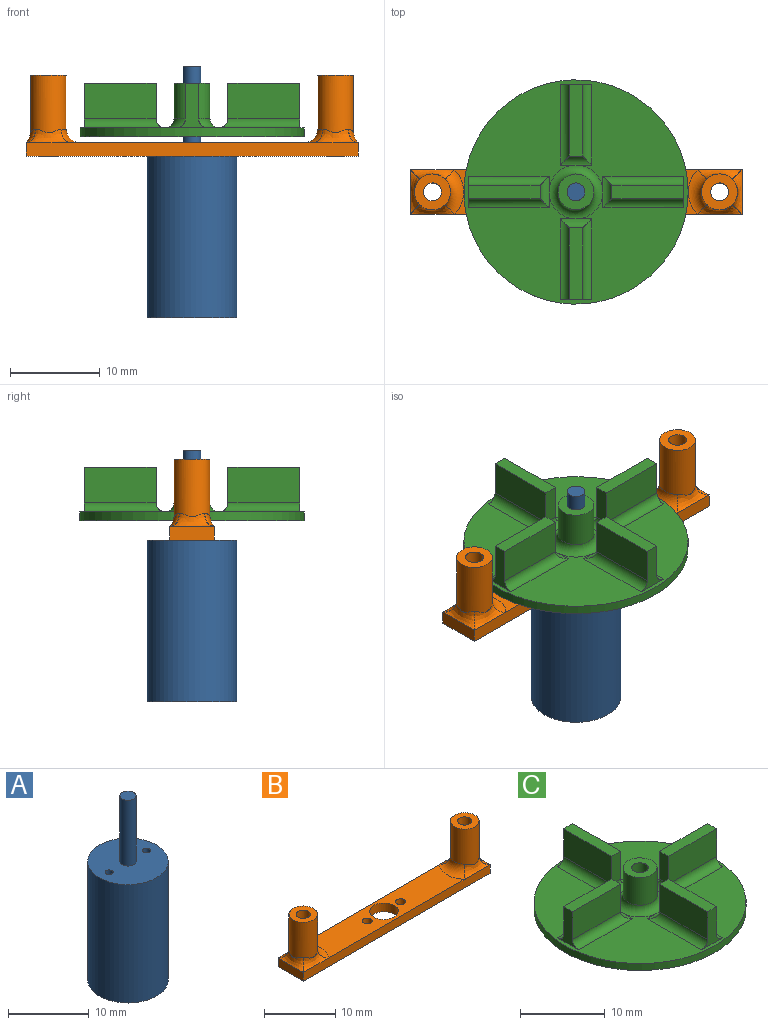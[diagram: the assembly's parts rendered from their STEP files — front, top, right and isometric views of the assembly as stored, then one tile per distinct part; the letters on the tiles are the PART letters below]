
ASSEMBLY  parts=3 mates=4
PART A: 9 faces, bbox 10x10x28 mm
  f0: cylinder r=5mm len=18mm, axis (0,0,-1), area 565.5mm2, adj f1,f2
  f1: plane 10x10mm, normal (0,0,1), area 73.8mm2, adj f0,f3,f5,f7
  f2: plane 10x10mm, normal (0,0,-1), area 78.5mm2, adj f0
  f3: cylinder r=1mm len=10mm, axis (0,0,-1), area 62.8mm2, adj f1,f4
  f4: plane 2x2mm, normal (0,0,1), area 3.1mm2, adj f3
  f5: cylinder r=0.5mm len=3mm, axis (0,0,1), area 9.4mm2, adj f1,f6
  f6: plane 1x1mm, normal (0,0,1), area 0.8mm2, adj f5
  f7: cylinder r=0.5mm len=3mm, axis (0,0,1), area 9.4mm2, adj f1,f8
  f8: plane 1x1mm, normal (0,0,1), area 0.8mm2, adj f7
PART B: 31 faces, bbox 38.7x7.3x9.2 mm
  f0: plane 0.05x0.05mm, normal (0,0,1), area 0mm2, adj f6,f11,f22
  f1: plane 0.05x0.05mm, normal (0,0,1), area 0mm2, adj f5,f6,f19
  f2: plane 0.05x0.05mm, normal (0,0,1), area 0mm2, adj f4,f11,f28
  f3: plane 27.1x5mm, normal (0,0,1), area 112.6mm2, adj f5,f8,f9,f10,f11,f23,f25
  f4: plane 5.2x1.7mm, normal (1,0,0), area 7.5mm2, adj f2,f5,f11,f13,f14,f30
  f5: plane 37.2x1.7mm, normal (0,1,0), area 55.5mm2, adj f1,f3,f4,f6,f13,f14,f21,f27
  f6: plane 5.2x1.7mm, normal (-1,0,0), area 7.5mm2, adj f0,f1,f5,f11,f14,f20
  f7: cylinder r=1mm len=9mm, axis (0,0,-1), area 56.5mm2, adj f14,f18
  f8: cylinder r=0.7mm len=1.5mm, axis (0,0,-1), area 6.6mm2, adj f3,f14
  f9: cylinder r=0.7mm len=1.5mm, axis (0,0,-1), area 6.6mm2, adj f3,f14
  f10: cylinder r=2mm len=4mm, axis (0,0,-1), area 18.8mm2, adj f3,f14
  f11: plane 37.2x1.7mm, normal (0,-1,0), area 55.5mm2, adj f0,f2,f3,f4,f6,f14,f24,f26
  f12: cylinder r=1mm len=9mm, axis (0,0,-1), area 56.5mm2, adj f14,f16
  f13: plane 0.05x0.05mm, normal (0,0,1), area 0mm2, adj f4,f5,f29
  f14: plane 37x5mm, normal (0,0,-1), area 163.1mm2, adj f4,f5,f6,f7,f8,f9,f10,f11
  f15: cylinder r=2mm len=6.38mm, axis (0,0,-1), area 77.2mm2, adj f16,f25,f26,f27,f28,f29,f30
  f16: plane 4x4mm, normal (0,0,1), area 9.4mm2, adj f12,f15
  f17: cylinder r=2mm len=6.38mm, axis (0,0,-1), area 77.2mm2, adj f18,f19,f20,f21,f22,f23,f24
  f18: plane 4x4mm, normal (0,0,1), area 9.4mm2, adj f7,f17
  f19: torus R=3.5mm, axis (0,0,1), area 0.1mm2, adj f1,f17,f20,f21
  f20: bspline ~5.2x1.62mm, area 5.8mm2, adj f6,f17,f19,f22
  f21: bspline ~5.2x1.62mm, area 5.8mm2, adj f5,f17,f19,f23
  f22: torus R=3.5mm, axis (0,0,1), area 0.1mm2, adj f0,f17,f20,f24
  f23: torus R=3.5mm, axis (0,0,1), area 9.5mm2, adj f3,f17,f21,f24
  f24: bspline ~5.2x1.62mm, area 5.8mm2, adj f11,f17,f22,f23
  f25: torus R=3.5mm, axis (0,0,1), area 9.5mm2, adj f3,f15,f26,f27
  f26: bspline ~5.2x1.62mm, area 5.8mm2, adj f11,f15,f25,f28
  f27: bspline ~5.2x1.62mm, area 5.8mm2, adj f5,f15,f25,f29
  f28: torus R=3.5mm, axis (0,0,1), area 0.1mm2, adj f2,f15,f26,f30
  f29: torus R=3.5mm, axis (0,0,1), area 0.1mm2, adj f13,f15,f27,f30
  f30: bspline ~5.2x1.62mm, area 5.8mm2, adj f4,f15,f28,f29
PART C: 39 faces, bbox 25x25x6 mm
  f0: cylinder r=12.5mm len=25mm, axis (0,0,-1), area 78.5mm2, adj f1,f2
  f1: plane 25x25mm, normal (0,0,1), area 336.6mm2, adj f0,f8,f14,f19,f24,f26,f27,f28
  f2: plane 25x25mm, normal (0,0,-1), area 487.9mm2, adj f0,f3
  f3: cylinder r=0.97mm len=6mm, axis (0,0,-1), area 36.8mm2, adj f2,f5
  f4: cylinder r=2mm len=4mm, axis (0,0,-1), area 50.3mm2, adj f5,f38
  f5: plane 4x4mm, normal (0,0,1), area 9.6mm2, adj f3,f4
  f6: plane 4x1.5mm, normal (1,0,0), area 6mm2, adj f7,f9,f10,f36
  f7: plane 8x4mm, normal (0,1,0), area 32mm2, adj f6,f8,f10,f37
  f8: plane 5x3.5mm, normal (-1,0,0), area 7.9mm2, adj f1,f7,f9,f10,f35,f37
  f9: plane 8x4mm, normal (0,-1,0), area 32mm2, adj f6,f8,f10,f35
  f10: plane 8x1.5mm, normal (0,0,1), area 12mm2, adj f6,f7,f8,f9
  f11: plane 8x4mm, normal (1,0,0), area 32mm2, adj f12,f14,f15,f32
  f12: plane 4x1.5mm, normal (0,1,0), area 6mm2, adj f11,f13,f15,f33
  f13: plane 8x4mm, normal (-1,0,0), area 32mm2, adj f12,f14,f15,f34
  f14: plane 5x3.5mm, normal (0,-1,0), area 7.9mm2, adj f1,f11,f13,f15,f32,f34
  f15: plane 8x1.5mm, normal (0,0,1), area 12mm2, adj f11,f12,f13,f14
  f16: plane 8x4mm, normal (0,1,0), area 32mm2, adj f17,f19,f20,f29
  f17: plane 4x1.5mm, normal (-1,0,0), area 6mm2, adj f16,f18,f20,f31
  f18: plane 8x4mm, normal (0,-1,0), area 32mm2, adj f17,f19,f20,f30
  f19: plane 5x3.5mm, normal (1,0,0), area 7.9mm2, adj f1,f16,f18,f20,f29,f30
  f20: plane 8x1.5mm, normal (0,0,1), area 12mm2, adj f16,f17,f18,f19
  f21: plane 8x4mm, normal (-1,0,0), area 32mm2, adj f22,f24,f25,f27
  f22: plane 4x1.5mm, normal (0,-1,0), area 6mm2, adj f21,f23,f25,f28
  f23: plane 8x4mm, normal (1,0,0), area 32mm2, adj f22,f24,f25,f26
  f24: plane 5x3.5mm, normal (0,1,0), area 7.9mm2, adj f1,f21,f23,f25,f26,f27
  f25: plane 8x1.5mm, normal (0,0,1), area 12mm2, adj f21,f22,f23,f24
  f26: cylinder r=1mm len=9mm, axis (0,1,0), area 13.1mm2, adj f1,f23,f24,f28
  f27: cylinder r=1mm len=9mm, axis (0,-1,0), area 13.1mm2, adj f1,f21,f24,f28
  f28: cylinder r=1mm len=3.5mm, axis (1,0,0), area 3.5mm2, adj f1,f22,f26,f27
  f29: cylinder r=1mm len=9mm, axis (-1,0,0), area 13.1mm2, adj f1,f16,f19,f31
  f30: cylinder r=1mm len=9mm, axis (1,0,0), area 13.1mm2, adj f1,f18,f19,f31
  f31: cylinder r=1mm len=3.5mm, axis (0,-1,0), area 3.5mm2, adj f1,f17,f29,f30
  f32: cylinder r=1mm len=9mm, axis (0,1,0), area 13.1mm2, adj f1,f11,f14,f33
  f33: cylinder r=1mm len=3.5mm, axis (-1,0,0), area 3.5mm2, adj f1,f12,f32,f34
  f34: cylinder r=1mm len=9mm, axis (0,-1,0), area 13.1mm2, adj f1,f13,f14,f33
  f35: cylinder r=1mm len=9mm, axis (1,0,0), area 13.1mm2, adj f1,f8,f9,f36
  f36: cylinder r=1mm len=3.5mm, axis (0,1,0), area 3.5mm2, adj f1,f6,f35,f37
  f37: cylinder r=1mm len=9mm, axis (-1,0,0), area 13.1mm2, adj f1,f7,f8,f36
  f38: torus R=3mm, axis (0,0,1), area 23.3mm2, adj f1,f4
PLACE A t=(4.28,10.92,-0.84)mm
PLACE B t=(4.28,10.92,17.16)mm
PLACE C t=(4.28,10.92,19.3)mm
MATE parallel B.f10 <-> A.f0  axis (0,0,-1) through (4.28,10.92,17.16)mm
MATE slider A.f3 <-> B.f10  axis (0,0,1) through (4.28,10.92,27.16)mm
MATE slider A.f3 <-> C.f3  axis (0,0,1) through (4.28,10.92,27.16)mm
MATE slider A.f7 <-> B.f8  axis (0,0,1) through (0.98,10.92,17.16)mm
